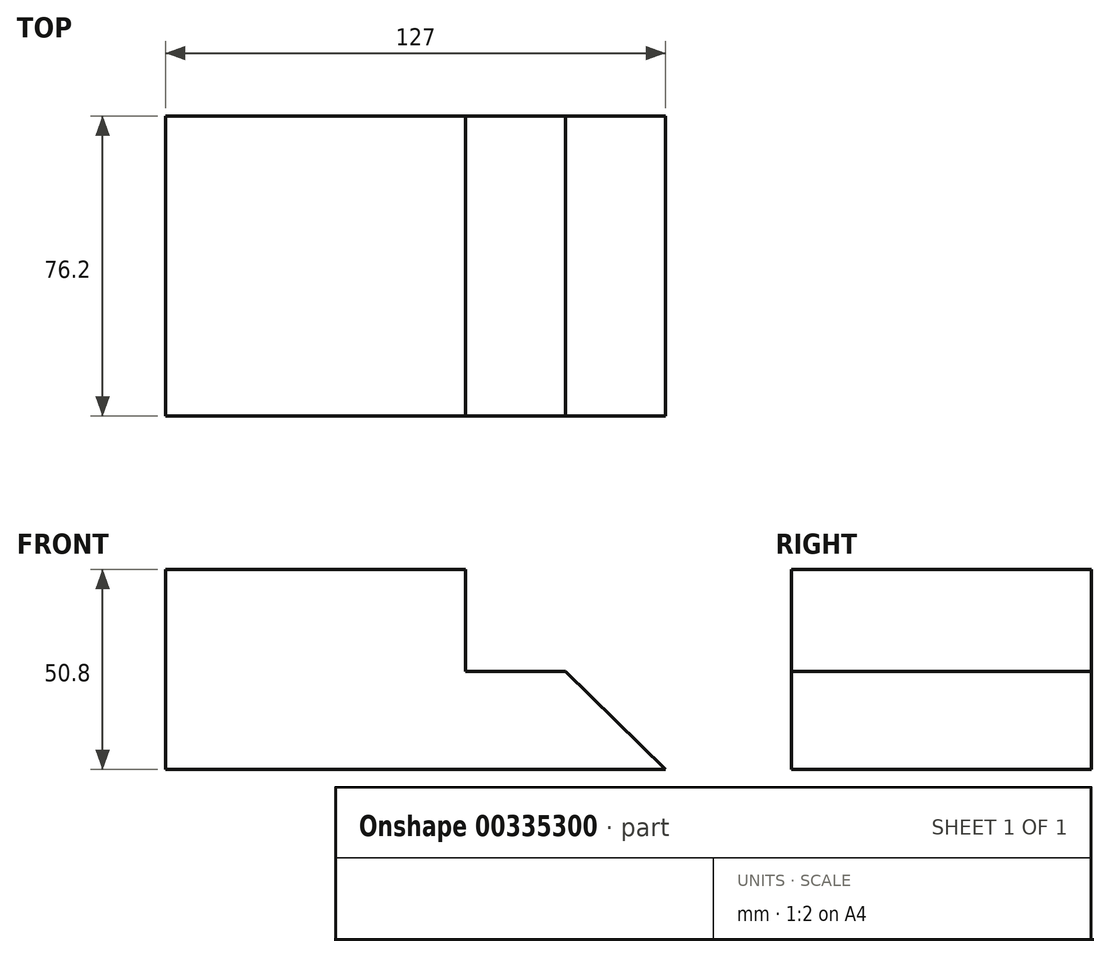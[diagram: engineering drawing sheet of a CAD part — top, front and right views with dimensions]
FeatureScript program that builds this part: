
annotation { "Feature Type Name" : "Feature", "Feature Type Description" : "" }
export const myFeature = defineFeature(function(context is Context, id is Id, definition is map)
    precondition{}
    {
        {
            var Q0;
            Q0=qCreatedBy(makeId("Front.planeOp"),FACE);
            var sketch = newSketch(context, id + "F0", { "sketchPlane" : qUnion([Q0])});
            skLineSegment(sketch, "E0", {"start": v(0, 0) * mm, "end": v(0, 50.8) * mm});
            skLineSegment(sketch, "E1", {"start": v(0, 50.8) * mm, "end": v(76.2, 50.8) * mm});
            skLineSegment(sketch, "E2", {"start": v(76.2, 50.8) * mm, "end": v(76.2, 24.9) * mm});
            skLineSegment(sketch, "E3", {"start": v(76.2, 24.9) * mm, "end": v(101.6, 24.9) * mm});
            skLineSegment(sketch, "E4", {"start": v(101.6, 24.9) * mm, "end": v(127, 0) * mm});
            skLineSegment(sketch, "E5", {"start": v(127, 0) * mm, "end": v(0, 0) * mm});
            skSolve(sketch);
        }
        {
            var Q0;
            Q0 = qSketchRegion(id + "F0", true);
            extrude(context, id + "F1", {"entities" : qUnion([Q0]), "depth" : 76.2 * mm});
        }
    });
